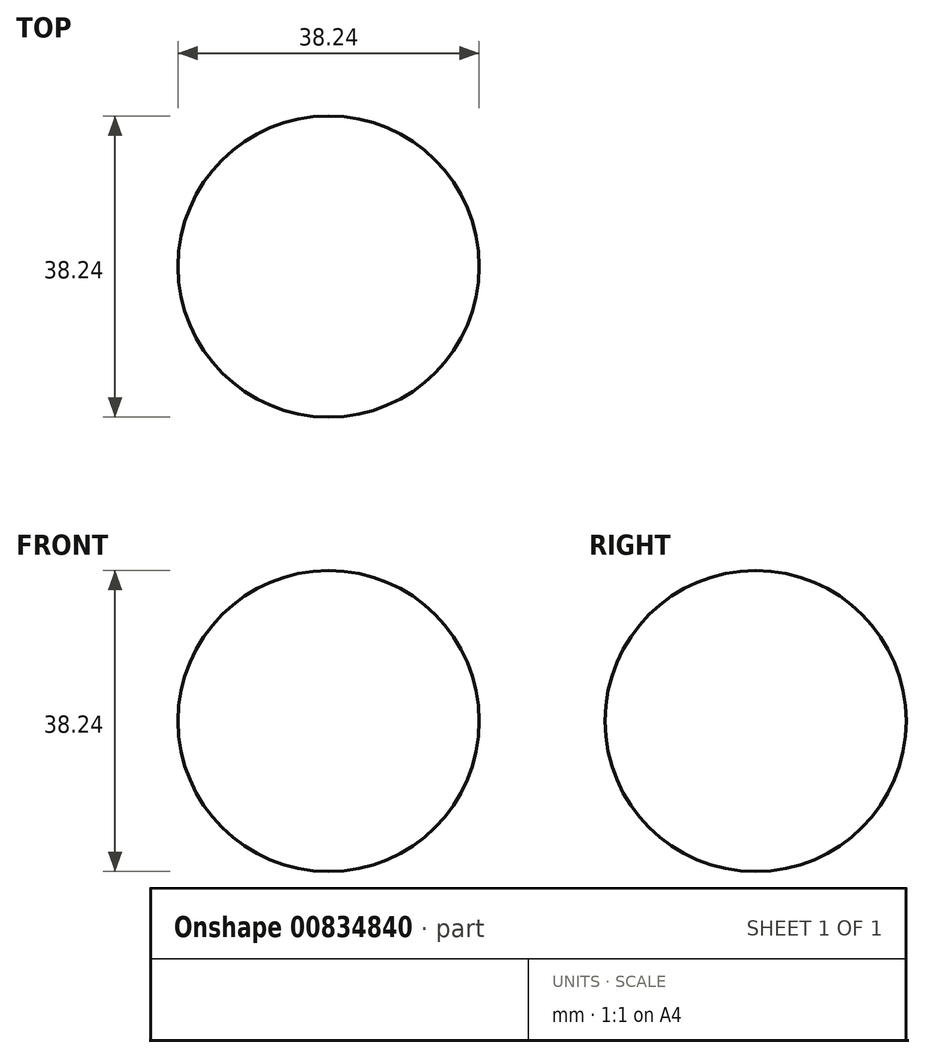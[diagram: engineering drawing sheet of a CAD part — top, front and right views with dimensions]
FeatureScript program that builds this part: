
annotation { "Feature Type Name" : "Feature", "Feature Type Description" : "" }
export const myFeature = defineFeature(function(context is Context, id is Id, definition is map)
    precondition{}
    {
        {
            var Q0;
            Q0=qCreatedBy(makeId("Top.planeOp"),FACE);
            var sketch = newSketch(context, id + "F0", { "sketchPlane" : qUnion([Q0])});
            skArc(sketch, "E0", {"start": v(0, 19.12) * mm, "mid": v(-19.12, 0) * mm, "end": v(0, -19.12) * mm});
            skLineSegment(sketch, "E1", {"start": v(0, 19.13) * mm, "end": v(0, -19.13) * mm});
            skPoint(sketch, "E2.orphan", {"position": v(0, 60.99) * mm});
            skSolve(sketch);
        }
        {
            var Q0;
            Q0 = qSketchRegion(id + "F0", true);
            var Q1;
            Q1=sQuery(id+"F0.wireOp",EDGE,"E1");
            revolve(context, id + "F1", {"surfaceOperationType" : NewSurfaceOperationType.NEW, "entities" : qUnion([Q0]), "axis" : qUnion([Q1]), "revolveType" : RevolveType.FULL});
        }
    });
